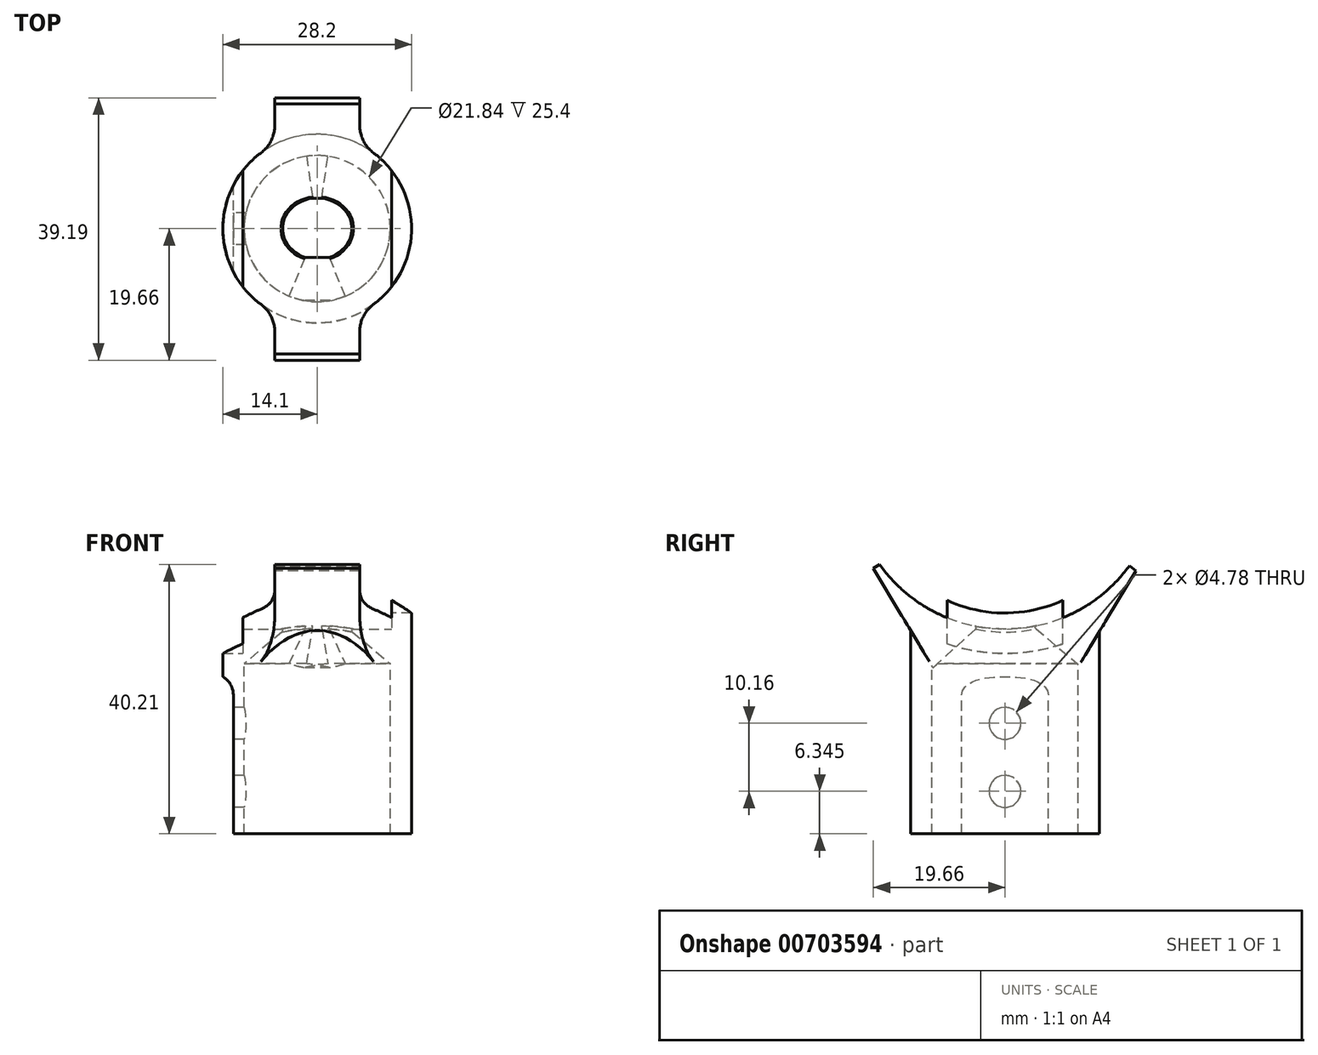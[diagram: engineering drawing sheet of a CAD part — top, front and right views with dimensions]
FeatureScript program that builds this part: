
annotation { "Feature Type Name" : "Feature", "Feature Type Description" : "" }
export const myFeature = defineFeature(function(context is Context, id is Id, definition is map)
    precondition{}
    {
        {
            var Q0;
            Q0=qCreatedBy(makeId("Front.planeOp"),FACE);
            var sketch = newSketch(context, id + "F0", { "sketchPlane" : qUnion([Q0])});
            skLineSegment(sketch, "E0", {"start": v(0, 0) * mm, "end": v(0, 9.52) * mm});
            skLineSegment(sketch, "E1", {"start": v(0, 9.52) * mm, "end": v(-14.1, 9.52) * mm});
            skLineSegment(sketch, "E2", {"start": v(-14.1, 9.53) * mm, "end": v(-14.1, -34.56) * mm});
            skLineSegment(sketch, "E3", {"start": v(-14.1, -34.56) * mm, "end": v(-10.92, -34.56) * mm});
            skLineSegment(sketch, "E4", {"start": v(-10.92, -34.56) * mm, "end": v(-10.92, -9.16) * mm});
            skLineSegment(sketch, "E5", {"start": v(-10.92, -9.16) * mm, "end": v(0, 0) * mm});
            skLineSegment(sketch, "E6", {"start": v(0, 0) * mm, "end": v(0, -49.1) * mm, "construction": true});
            skSolve(sketch);
        }
        {
            var Q0;
            Q0=makeQuery(id+"F0.imprint","IMPRINT",FACE,{"disambiguationData":[TD([[makeQuery(id+"F0.imprint","IMPRINT",EDGE,{"derivedFrom":sQuery(id+"F0.wireOp",EDGE,"E0")}),1.0]])]});
            var Q1;
            Q1=sQuery(id+"F0.wireOp",EDGE,"E6");
            revolve(context, id + "F1", {"surfaceOperationType" : NewSurfaceOperationType.NEW, "entities" : qUnion([Q0]), "axis" : qUnion([Q1]), "revolveType" : RevolveType.FULL});
        }
        {
            var Q0;
            Q0=makeQuery(id+"F1.opRevolve","SWEPT_EDGE",EDGE,{"disambiguationData":[OSD([sQuery(id+"F0.wireOp",EDGE,"E1"),sQuery(id+"F0.wireOp",EDGE,"E2")])]});
            fillet(context, id + "F2", {"entities" : qUnion([Q0]), "radius" : 2.4 * mm, "tangentPropagation" : true, "allowEdgeOverflow" : false});
        }
        {
            var Q0;
            Q0=qCreatedBy(makeId("Front.planeOp"),FACE);
            var sketch = newSketch(context, id + "F3", { "sketchPlane" : qUnion([Q0])});
            skLineSegment(sketch, "E7", {"start": v(-76.7, 0) * mm, "end": v(76.07, 0) * mm});
            skLineSegment(sketch, "E8", {"start": v(14.08, -10.67) * mm, "end": v(11.62, -10.67) * mm});
            skLineSegment(sketch, "E9", {"start": v(11.62, -10.67) * mm, "end": v(11.62, -36.07) * mm});
            skLineSegment(sketch, "E10", {"start": v(14.11, 2.42) * mm, "end": v(14.11, -36.07) * mm});
            skLineSegment(sketch, "E11", {"start": v(-15.7, -10.67) * mm, "end": v(-18.86, -10.67) * mm});
            skLineSegment(sketch, "E12", {"start": v(-10.92, -10.67) * mm, "end": v(-10.92, -36.07) * mm});
            skLineSegment(sketch, "E13", {"start": v(-18.86, -10.67) * mm, "end": v(-18.86, -38.6) * mm});
            skLineSegment(sketch, "E14", {"start": v(-12.53, -38.6) * mm, "end": v(-18.86, -38.6) * mm});
            skLineSegment(sketch, "E15", {"start": v(-12.53, -13.84) * mm, "end": v(-12.53, -38.6) * mm});
            skPoint(sketch, "E16.visualSharp", {"position": v(-12.53, -10.67) * mm});
            skArc(sketch, "E16.filletArc", {"start": v(-12.53, -13.84) * mm, "mid": v(-13.46, -11.6) * mm, "end": v(-15.7, -10.67) * mm});
            skSolve(sketch);
        }
        {
            var Q0;
            Q0 = qSketchRegion(id + "F3", true);
            extrude(context, id + "F4", {"entities" : qUnion([Q0]), "operationType" : NewBodyOperationType.REMOVE, "oppositeDirection" : true, "depth" : 25.4 * mm, "offsetDistance" : 25.4 * mm, "hasSecondDirection" : true, "secondDirectionOppositeDirection" : false, "secondDirectionDepth" : 25.4 * mm});
        }
        {
            var Q0;
            Q0=makeQuery(id+"F4.boolean.opBoolean","COPY",FACE,{"derivedFrom":makeQuery(id+"F4.opExtrude","SWEPT_FACE",FACE,{"disambiguationData":[OSD([sQuery(id+"F3.wireOp",EDGE,"E15")])]})});
            var sketch = newSketch(context, id + "F5", { "sketchPlane" : qUnion([Q0])});
            skLineSegment(sketch, "E17", {"start": v(0, -13.84) * mm, "end": v(0, -36.42) * mm, "construction": true});
            skCircle(sketch, "E18", {"center": v(0, -28.21) * mm, "radius": 2.39 * mm});
            skCircle(sketch, "E19", {"center": v(0, -18.05) * mm, "radius": 2.39 * mm});
            skSolve(sketch);
        }
        {
            var Q0;
            Q0 = qSketchRegion(id + "F5", true);
            extrude(context, id + "F6", {"entities" : qUnion([Q0]), "operationType" : NewBodyOperationType.REMOVE, "oppositeDirection" : true, "depth" : 6.35 * mm, "offsetDistance" : 25.4 * mm});
        }
        {
            var Q0;
            Q0=qCreatedBy(makeId("Right.planeOp"),FACE);
            var sketch = newSketch(context, id + "F7", { "sketchPlane" : qUnion([Q0])});
            skLineSegment(sketch, "E20", {"start": v(0, 78.93) * mm, "end": v(0, -80.28) * mm});
            skLineSegment(sketch, "E21", {"start": v(0, 0) * mm, "end": v(0, 20.28) * mm, "construction": true});
            skCircle(sketch, "E22", {"center": v(0, 20.28) * mm, "radius": 23.03 * mm});
            skLineSegment(sketch, "E23", {"start": v(0, 0) * mm, "end": v(-10.75, -9.76) * mm});
            skLineSegment(sketch, "E24", {"start": v(0, 0) * mm, "end": v(11.07, -9.4) * mm});
            skLineSegment(sketch, "E25", {"start": v(11.07, -9.4) * mm, "end": v(21.53, 8.03) * mm});
            skLineSegment(sketch, "E26", {"start": v(-10.75, -9.76) * mm, "end": v(-21.21, 7.66) * mm});
            skLineSegment(sketch, "E27", {"start": v(21.53, 8.03) * mm, "end": v(-21.21, 7.66) * mm});
            skLineSegment(sketch, "E28", {"start": v(21.53, 8.03) * mm, "end": v(15.62, 7.98) * mm});
            skLineSegment(sketch, "E29", {"start": v(-21.21, 7.66) * mm, "end": v(-15.3, 7.71) * mm});
            skLineSegment(sketch, "E30", {"start": v(-15.3, 7.71) * mm, "end": v(-19.66, 5.08) * mm});
            skLineSegment(sketch, "E31", {"start": v(15.62, 7.98) * mm, "end": v(19.53, 4.7) * mm});
            skSolve(sketch);
        }
        {
            var Q0;
            {var subQ1=sQuery(id+"F7.wireOp",EDGE,"E24");Q0=makeQuery(id+"F7.imprint","IMPRINT",FACE,{"disambiguationData":[TD([[makeQuery(id+"F7.imprint","IMPRINT",EDGE,{"derivedFrom":subQ1}),1.0]])]});}
            var Q1;
            {var subQ4=sQuery(id+"F7.wireOp",EDGE,"E23");Q1=makeQuery(id+"F7.imprint","IMPRINT",FACE,{"disambiguationData":[TD([[makeQuery(id+"F7.imprint","IMPRINT",EDGE,{"derivedFrom":subQ4}),-1.0]])]});}
            extrude(context, id + "F8", {"entities" : qUnion([Q0, Q1]), "operationType" : NewBodyOperationType.ADD, "depth" : 6.35 * mm, "offsetDistance" : 25.4 * mm, "hasSecondDirection" : true, "secondDirectionOppositeDirection" : true, "secondDirectionDepth" : 6.35 * mm});
        }
        {
            var Q0;
            Q0=qCreatedBy(makeId("Right.planeOp"),FACE);
            var sketch = newSketch(context, id + "F9", { "sketchPlane" : qUnion([Q0])});
            skCircle(sketch, "E32", {"center": v(0, 19.05) * mm, "radius": 23.03 * mm});
            skSolve(sketch);
        }
        {
            var Q0;
            Q0 = qSketchRegion(id + "F9", true);
            extrude(context, id + "F10", {"entities" : qUnion([Q0]), "operationType" : NewBodyOperationType.REMOVE, "oppositeDirection" : true, "depth" : 25.4 * mm, "offsetDistance" : 25.4 * mm, "hasSecondDirection" : true, "secondDirectionOppositeDirection" : false, "secondDirectionDepth" : 11.13 * mm});
        }
        {
            var Q0;
            Q0=makeQuery(id+"F8.boolean.opBoolean","INTERSECT",EDGE,{"derivedFrom":[makeQuery(id+"F1.opRevolve","SWEPT_FACE",FACE,{"disambiguationData":[OSD([sQuery(id+"F0.wireOp",EDGE,"E2")])]}),makeQuery(id+"F8.opExtrude","CAP_FACE",FACE,{"disambiguationData":[OSD([sQuery(id+"F7.wireOp",EDGE,"E22"),sQuery(id+"F7.wireOp",EDGE,"E24"),sQuery(id+"F7.wireOp",EDGE,"E25"),sQuery(id+"F7.wireOp",EDGE,"E31")])],"isStart":true})]});
            var Q1;
            Q1=makeQuery(id+"F8.boolean.opBoolean","INTERSECT",EDGE,{"derivedFrom":[makeQuery(id+"F1.opRevolve","SWEPT_FACE",FACE,{"disambiguationData":[OSD([sQuery(id+"F0.wireOp",EDGE,"E2")])]}),makeQuery(id+"F8.opExtrude","CAP_FACE",FACE,{"disambiguationData":[OSD([sQuery(id+"F7.wireOp",EDGE,"E22"),sQuery(id+"F7.wireOp",EDGE,"E23"),sQuery(id+"F7.wireOp",EDGE,"E26"),sQuery(id+"F7.wireOp",EDGE,"E30")])],"isStart":true})]});
            var Q2;
            Q2=makeQuery(id+"F8.boolean.opBoolean","INTERSECT",EDGE,{"derivedFrom":[makeQuery(id+"F1.opRevolve","SWEPT_FACE",FACE,{"disambiguationData":[OSD([sQuery(id+"F0.wireOp",EDGE,"E2")])]}),makeQuery(id+"F8.opExtrude","CAP_FACE",FACE,{"disambiguationData":[OSD([sQuery(id+"F7.wireOp",EDGE,"E22"),sQuery(id+"F7.wireOp",EDGE,"E23"),sQuery(id+"F7.wireOp",EDGE,"E26"),sQuery(id+"F7.wireOp",EDGE,"E30")])],"isStart":false})]});
            var Q3;
            Q3=makeQuery(id+"F8.boolean.opBoolean","INTERSECT",EDGE,{"derivedFrom":[makeQuery(id+"F1.opRevolve","SWEPT_FACE",FACE,{"disambiguationData":[OSD([sQuery(id+"F0.wireOp",EDGE,"E2")])]}),makeQuery(id+"F8.opExtrude","CAP_FACE",FACE,{"disambiguationData":[OSD([sQuery(id+"F7.wireOp",EDGE,"E22"),sQuery(id+"F7.wireOp",EDGE,"E24"),sQuery(id+"F7.wireOp",EDGE,"E25"),sQuery(id+"F7.wireOp",EDGE,"E31")])],"isStart":false})]});
            fillet(context, id + "F11", {"entities" : qUnion([Q0, Q1, Q2, Q3]), "radius" : 5.08 * mm, "tangentPropagation" : true, "allowEdgeOverflow" : false});
        }
        {
            var Q0;
            Q0=qCreatedBy(makeId("Right.planeOp"),FACE);
            var sketch = newSketch(context, id + "F12", { "sketchPlane" : qUnion([Q0])});
            skCircle(sketch, "E33", {"center": v(0, 19.05) * mm, "radius": 20.64 * mm});
            skSolve(sketch);
        }
        {
            var Q0;
            Q0 = qSketchRegion(id + "F12", true);
            extrude(context, id + "F13", {"entities" : qUnion([Q0]), "operationType" : NewBodyOperationType.REMOVE, "depth" : 25.4 * mm, "offsetDistance" : 25.4 * mm});
        }
        {
            var Q0;
            Q0=qCreatedBy(makeId("Right.planeOp"),FACE);
            cPlane(context, id + "F14", {"entities" : qUnion([Q0]), "cplaneType" : CPlaneType.OFFSET, "offset" : 11.13 * mm, "oppositeDirection" : true, "width" : 152.4 * mm, "height" : 152.4 * mm});
        }
        {
            var Q0;
            Q0=qCreatedBy(id+"F14.planeOp",FACE);
            var sketch = newSketch(context, id + "F15", { "sketchPlane" : qUnion([Q0])});
            skCircle(sketch, "E34", {"center": v(0, 19.05) * mm, "radius": 26.67 * mm});
            skSolve(sketch);
        }
        {
            var Q0;
            Q0 = qSketchRegion(id + "F15", true);
            extrude(context, id + "F16", {"entities" : qUnion([Q0]), "operationType" : NewBodyOperationType.REMOVE, "oppositeDirection" : true, "depth" : 25.4 * mm, "offsetDistance" : 25.4 * mm});
        }
        {
            var Q0;
            Q0=makeQuery(id+"F10.boolean.opBoolean","INTERSECT",EDGE,{"disambiguationData":[OD(1.0)],"derivedFrom":[makeQuery(id+"F1.opRevolve","SWEPT_FACE",FACE,{"disambiguationData":[OSD([sQuery(id+"F0.wireOp",EDGE,"E5")])]}),makeQuery(id+"F10.opExtrude","SWEPT_FACE",FACE,{"disambiguationData":[OSD([sQuery(id+"F9.wireOp",EDGE,"E32")])]})]});
            var Q1;
            Q1=makeQuery(id+"F10.boolean.opBoolean","INTERSECT",EDGE,{"disambiguationData":[OD(0.0)],"derivedFrom":[makeQuery(id+"F1.opRevolve","SWEPT_FACE",FACE,{"disambiguationData":[OSD([sQuery(id+"F0.wireOp",EDGE,"E5")])]}),makeQuery(id+"F10.opExtrude","SWEPT_FACE",FACE,{"disambiguationData":[OSD([sQuery(id+"F9.wireOp",EDGE,"E32")])]})]});
            var Q2;
            Q2=makeQuery(id+"F10.boolean.opBoolean","INTERSECT",EDGE,{"derivedFrom":[makeQuery(id+"F8.opExtrude","SWEPT_FACE",FACE,{"disambiguationData":[OSD([sQuery(id+"F7.wireOp",EDGE,"E24")])]}),makeQuery(id+"F10.opExtrude","SWEPT_FACE",FACE,{"disambiguationData":[OSD([sQuery(id+"F9.wireOp",EDGE,"E32")])]})]});
            var Q3;
            Q3=makeQuery(id+"F10.boolean.opBoolean","INTERSECT",EDGE,{"derivedFrom":[makeQuery(id+"F8.opExtrude","SWEPT_FACE",FACE,{"disambiguationData":[OSD([sQuery(id+"F7.wireOp",EDGE,"E23")])]}),makeQuery(id+"F10.opExtrude","SWEPT_FACE",FACE,{"disambiguationData":[OSD([sQuery(id+"F9.wireOp",EDGE,"E32")])]})]});
            fillet(context, id + "F17", {"entities" : qUnion([Q0, Q1, Q2, Q3]), "radius" : 0.25 * mm, "tangentPropagation" : true, "allowEdgeOverflow" : false});
        }
    });
